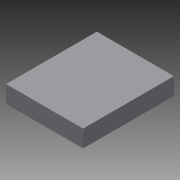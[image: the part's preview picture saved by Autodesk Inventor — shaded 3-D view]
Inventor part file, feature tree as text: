
AUTODESK INVENTOR PART (.ipt)
format: ipt  version: 2015 (Build 190159000, 159)  size: 68,096 bytes
history: native  units: in
note: dims shown in document units (in); Inventor stores cm internally (conversion verified against a paired STEP export)
features: extrude x1, sketch x1
ambient origin geometry x8: Origin, YZ Plane, XZ Plane, XY Plane, X Axis, Y Axis, Z Axis, Center Point
bodies: Solid1 (feature_tree)
feature tree (2):
  extrude  "Extrusion1"  Depth=31.8333in
  sketch  "Sketch1"  dims[d0=27.0in d1=31.8333in d2=6.0in d3=0.0in]
